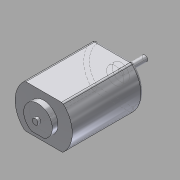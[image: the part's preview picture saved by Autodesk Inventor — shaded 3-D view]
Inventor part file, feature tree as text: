
AUTODESK INVENTOR PART (.ipt)
format: ipt  version: 2015 (Build 190159000, 159)  size: 138,752 bytes
history: native  units: in
note: dims shown in document units (in); Inventor stores cm internally (conversion verified against a paired STEP export)
features: sketch x5, other x3
ambient origin geometry x8: Origin, YZ Plane, XZ Plane, XY Plane, X Axis, Y Axis, Z Axis, Center Point
bodies: Solid1 (feature_tree)
feature tree (8):
  other  "motor.ipt"
  other  "Solid1::motor.ipt"
  other  "TaggingFeature1"
  sketch  "Sketch1"  dims[d0=0.3937in]
  sketch  "Sketch2"
  sketch  "Sketch3"
  sketch  "Sketch4"
  sketch  "Sketch5"
